# Revit family: Sky Væg
name_source: partatom
category: Lighting Fixtures
revit_build: Autodesk Revit 2015 (Build: 20140606_1530(x64)
units: mm (PartAtom-declared; Revit-internal decimal feet)

## types (1)
- Sky Wall
    Color Filter = 16777215
    Date = 21.03.2016
    Description = Sky Væg
    Diffuser Material = 0 mm  [stored 0 ft]
    Dimming Lamp Color Temperature Shift = <None>
    Finish Material = Aluminum Silver grey (MW300D)
    Foreclosure Material = Clear Polycarbonate with UV-resistant acrylic
    Installation Instructions URL = http://www.focus-lighting.dk
    Light Source Symbol Size = 600 mm
    Manufacturer = Focus Lighting A/S
    Material = 0 mm  [stored 0 ft]
    Product Family = Outdoors
    Product Group = Sky Wall
    Product URL = http://www.focus-lighting.dk
    Revit Object URL = http://www.newbim.info
    Technical Description URL = http://www.focus-lighting.dk
    Type Image = Perspective View 2.jpg
    URL = http://focus-lighting.dk
    Weight = 9.7 kg

note: [stored X ft] marks values corroborated as IEEE doubles in the binary element streams (Revit-internal decimal feet)

## geometry (parser evidence)
native form markers: Sweep x1
no freeform markers — native parametric forms only
